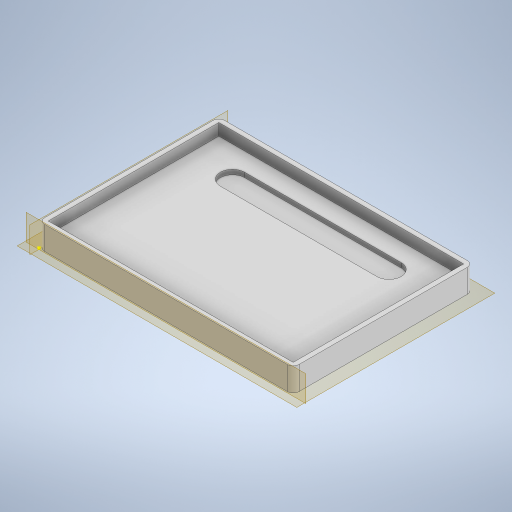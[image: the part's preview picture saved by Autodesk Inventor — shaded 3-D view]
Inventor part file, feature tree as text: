
AUTODESK INVENTOR PART (.ipt)
format: ipt  version: 2024 (Build 280153000, 153)  size: 281,600 bytes
history: native  units: mm
features: sketch x4, extrude x3, fillet x1
ambient origin geometry x8: Origin, YZ Plane, XZ Plane, XY Plane, X Axis, Y Axis, Z Axis, Center Point
bodies: Solid1 (feature_tree)
feature tree (8):
  sketch  "Sketch1"  dims[d0=65.0mm d1=46.0mm]
  extrude  "Extrusion1"  Depth=46.0mm
  extrude  "Extrusion2"  TaperAngle=0.0deg  [1 undecoded]
  extrude  "Extrusion4"  TaperAngle=0.0deg  [1 undecoded]
  fillet  "Fillet2"  Radius=9.0mm
  sketch  "Sketch2"  dims[d2=3.0mm d3=0.0mm]
  sketch  "Sketch3"  dims[d5=6.2mm d6=0.0mm d7=9.0mm]
  sketch  "Sketch6"  dims[d8=1.2mm d9=0.0mm d13=1.2mm d14=3.0mm d15=0.0mm d16=1.5mm d18=40.0mm d19=0.0mm d11=0.5mm d12=0.872665mm]
note: 2 required parameter values undecoded (feature->parameter linkage not recoverable at this tier; creation-order binding heuristic only, values carry confidence <= 0.55)
